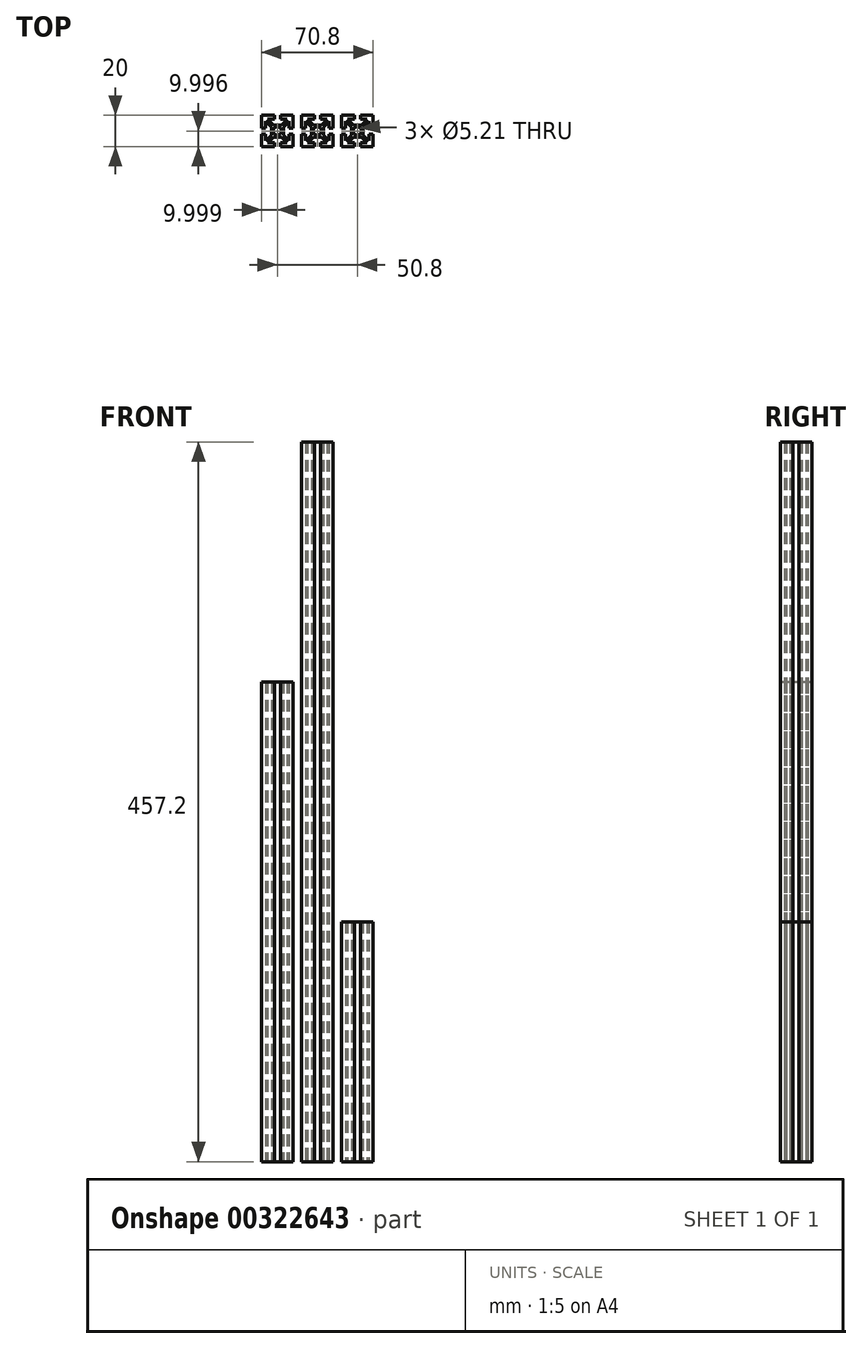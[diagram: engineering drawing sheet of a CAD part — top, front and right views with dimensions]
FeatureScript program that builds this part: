
annotation { "Feature Type Name" : "Feature", "Feature Type Description" : "" }
export const myFeature = defineFeature(function(context is Context, id is Id, definition is map)
    precondition{}
    {
        {
            var Q0;
            Q0=qCreatedBy(makeId("Top.planeOp"),FACE);
            var sketch = newSketch(context, id + "F0", { "sketchPlane" : qUnion([Q0])});
            skCircle(sketch, "E0", {"center": v(-14.24, 3.76) * mm, "radius": 2.6 * mm});
            skLineSegment(sketch, "E1.bottom", {"start": v(-18.05, 7.57) * mm, "end": v(-10.43, 7.57) * mm, "construction": true});
            skLineSegment(sketch, "E1.top", {"start": v(-18.05, -0.05) * mm, "end": v(-10.43, -0.05) * mm, "construction": true});
            skLineSegment(sketch, "E1.left", {"start": v(-18.05, 7.57) * mm, "end": v(-18.05, -0.05) * mm, "construction": true});
            skLineSegment(sketch, "E1.right", {"start": v(-10.43, 7.57) * mm, "end": v(-10.43, -0.05) * mm, "construction": true});
            skPoint(sketch, "E2", {"position": v(-18.05, 3.76) * mm});
            skPoint(sketch, "E3", {"position": v(-14.24, 7.57) * mm});
            skLineSegment(sketch, "E4", {"start": v(-16.78, 7.57) * mm, "end": v(-11.7, 7.57) * mm});
            skLineSegment(sketch, "E5", {"start": v(-11.7, 7.57) * mm, "end": v(-8.05, 11.22) * mm});
            skLineSegment(sketch, "E6", {"start": v(-8.05, 11.22) * mm, "end": v(-12.34, 11.22) * mm});
            skLineSegment(sketch, "E7", {"start": v(-12.34, 11.22) * mm, "end": v(-12.34, 13.76) * mm});
            skLineSegment(sketch, "E8", {"start": v(-12.34, 13.76) * mm, "end": v(-4.24, 13.76) * mm});
            skLineSegment(sketch, "E9", {"start": v(-4.24, 13.76) * mm, "end": v(-4.24, 5.66) * mm});
            skLineSegment(sketch, "E10", {"start": v(-4.24, 5.66) * mm, "end": v(-6.78, 5.66) * mm});
            skLineSegment(sketch, "E11", {"start": v(-6.78, 5.66) * mm, "end": v(-6.78, 9.95) * mm});
            skLineSegment(sketch, "E12", {"start": v(-6.78, 9.95) * mm, "end": v(-10.43, 6.3) * mm});
            skLineSegment(sketch, "E13", {"start": v(-10.43, 6.3) * mm, "end": v(-10.43, 1.22) * mm});
            skLineSegment(sketch, "E14", {"start": v(-10.43, 1.22) * mm, "end": v(-6.78, -2.43) * mm});
            skLineSegment(sketch, "E15", {"start": v(-6.78, -2.43) * mm, "end": v(-6.78, 1.85) * mm});
            skLineSegment(sketch, "E16", {"start": v(-6.78, 1.85) * mm, "end": v(-4.24, 1.85) * mm});
            skLineSegment(sketch, "E17", {"start": v(-4.24, 1.85) * mm, "end": v(-4.24, -6.24) * mm});
            skLineSegment(sketch, "E18", {"start": v(-4.24, -6.24) * mm, "end": v(-12.34, -6.24) * mm});
            skLineSegment(sketch, "E19", {"start": v(-12.34, -6.24) * mm, "end": v(-12.34, -3.7) * mm});
            skLineSegment(sketch, "E20", {"start": v(-12.34, -3.7) * mm, "end": v(-8.05, -3.7) * mm});
            skLineSegment(sketch, "E21", {"start": v(-8.05, -3.7) * mm, "end": v(-11.7, -0.05) * mm});
            skLineSegment(sketch, "E22", {"start": v(-11.7, -0.05) * mm, "end": v(-16.78, -0.05) * mm});
            skLineSegment(sketch, "E23", {"start": v(-16.78, -0.05) * mm, "end": v(-20.43, -3.7) * mm});
            skLineSegment(sketch, "E24", {"start": v(-20.43, -3.7) * mm, "end": v(-16.15, -3.7) * mm});
            skLineSegment(sketch, "E25", {"start": v(-16.15, -3.7) * mm, "end": v(-16.15, -6.24) * mm});
            skLineSegment(sketch, "E26", {"start": v(-16.15, -6.24) * mm, "end": v(-24.24, -6.24) * mm});
            skLineSegment(sketch, "E27", {"start": v(-24.24, -6.24) * mm, "end": v(-24.24, 1.85) * mm});
            skLineSegment(sketch, "E28", {"start": v(-24.24, 1.85) * mm, "end": v(-21.7, 1.85) * mm});
            skLineSegment(sketch, "E29", {"start": v(-21.7, 1.85) * mm, "end": v(-21.7, -2.43) * mm});
            skLineSegment(sketch, "E30", {"start": v(-21.7, -2.43) * mm, "end": v(-18.05, 1.22) * mm});
            skLineSegment(sketch, "E31", {"start": v(-18.05, 1.22) * mm, "end": v(-18.05, 6.3) * mm});
            skLineSegment(sketch, "E32", {"start": v(-18.05, 6.3) * mm, "end": v(-21.7, 9.95) * mm});
            skLineSegment(sketch, "E33", {"start": v(-21.7, 9.95) * mm, "end": v(-21.7, 5.66) * mm});
            skLineSegment(sketch, "E34", {"start": v(-21.7, 5.66) * mm, "end": v(-24.24, 5.66) * mm});
            skLineSegment(sketch, "E35", {"start": v(-24.24, 5.66) * mm, "end": v(-24.24, 13.76) * mm});
            skLineSegment(sketch, "E36", {"start": v(-24.24, 13.76) * mm, "end": v(-16.15, 13.76) * mm});
            skLineSegment(sketch, "E37", {"start": v(-16.15, 13.76) * mm, "end": v(-16.15, 11.22) * mm});
            skLineSegment(sketch, "E38", {"start": v(-16.15, 11.22) * mm, "end": v(-20.43, 11.22) * mm});
            skLineSegment(sketch, "E39", {"start": v(-20.43, 11.22) * mm, "end": v(-16.78, 7.57) * mm});
            skLineSegment(sketch, "E40", {"start": v(-16.15, 13.76) * mm, "end": v(-12.34, 13.76) * mm, "construction": true});
            skLineSegment(sketch, "E41", {"start": v(-4.24, 5.66) * mm, "end": v(-4.24, 1.85) * mm, "construction": true});
            skLineSegment(sketch, "E42", {"start": v(-12.34, -6.24) * mm, "end": v(-16.15, -6.24) * mm, "construction": true});
            skLineSegment(sketch, "E43", {"start": v(-24.24, 1.85) * mm, "end": v(-24.24, 5.66) * mm, "construction": true});
            skPoint(sketch, "E44", {"position": v(-24.24, 3.76) * mm});
            skPoint(sketch, "E45", {"position": v(-14.24, 13.76) * mm});
            skPoint(sketch, "E46", {"position": v(-4.24, 3.76) * mm});
            skPoint(sketch, "E47", {"position": v(-14.24, -6.24) * mm});
            skPoint(sketch, "E48.1.0.0", {"position": v(21.16, 3.76) * mm});
            skLineSegment(sketch, "E48.1.0.1", {"start": v(1.16, 13.76) * mm, "end": v(9.25, 13.76) * mm});
            skPoint(sketch, "E48.1.0.2", {"position": v(11.16, 13.76) * mm});
            skPoint(sketch, "E48.1.0.3", {"position": v(1.16, 3.76) * mm});
            skPoint(sketch, "E48.1.0.4", {"position": v(11.16, -6.24) * mm});
            skCircle(sketch, "E48.1.0.5", {"center": v(11.16, 3.76) * mm, "radius": 2.6 * mm});
            skPoint(sketch, "E48.1.0.6", {"position": v(11.16, 7.57) * mm});
            skLineSegment(sketch, "E48.1.0.7", {"start": v(18.62, -2.43) * mm, "end": v(18.62, 1.85) * mm});
            skPoint(sketch, "E48.1.0.8", {"position": v(7.35, 3.76) * mm});
            skLineSegment(sketch, "E48.1.0.9", {"start": v(7.35, -0.05) * mm, "end": v(14.97, -0.05) * mm, "construction": true});
            skLineSegment(sketch, "E48.1.0.10", {"start": v(21.16, 13.76) * mm, "end": v(21.16, 5.66) * mm});
            skLineSegment(sketch, "E48.1.0.11", {"start": v(13.06, 13.76) * mm, "end": v(21.16, 13.76) * mm});
            skLineSegment(sketch, "E48.1.0.12", {"start": v(18.62, 5.66) * mm, "end": v(18.62, 9.95) * mm});
            skLineSegment(sketch, "E48.1.0.13", {"start": v(21.16, 1.85) * mm, "end": v(21.16, -6.24) * mm});
            skLineSegment(sketch, "E48.1.0.14", {"start": v(21.16, -6.24) * mm, "end": v(13.06, -6.24) * mm});
            skLineSegment(sketch, "E48.1.0.15", {"start": v(9.25, -6.24) * mm, "end": v(1.16, -6.24) * mm});
            skLineSegment(sketch, "E48.1.0.16", {"start": v(1.16, 5.66) * mm, "end": v(1.16, 13.76) * mm});
            skLineSegment(sketch, "E48.1.0.17", {"start": v(1.16, -6.24) * mm, "end": v(1.16, 1.85) * mm});
            skLineSegment(sketch, "E48.1.0.18", {"start": v(3.7, 1.85) * mm, "end": v(3.7, -2.43) * mm});
            skLineSegment(sketch, "E48.1.0.19", {"start": v(14.97, 1.22) * mm, "end": v(18.62, -2.43) * mm});
            skLineSegment(sketch, "E48.1.0.20", {"start": v(3.7, 9.95) * mm, "end": v(3.7, 5.66) * mm});
            skLineSegment(sketch, "E48.1.0.21", {"start": v(14.97, 7.57) * mm, "end": v(14.97, -0.05) * mm, "construction": true});
            skLineSegment(sketch, "E48.1.0.22", {"start": v(7.35, 7.57) * mm, "end": v(7.35, -0.05) * mm, "construction": true});
            skLineSegment(sketch, "E48.1.0.23", {"start": v(13.7, -0.05) * mm, "end": v(8.62, -0.05) * mm});
            skLineSegment(sketch, "E48.1.0.24", {"start": v(7.35, 7.57) * mm, "end": v(14.97, 7.57) * mm, "construction": true});
            skLineSegment(sketch, "E48.1.0.25", {"start": v(13.7, 7.57) * mm, "end": v(17.35, 11.22) * mm});
            skLineSegment(sketch, "E48.1.0.26", {"start": v(7.35, 1.22) * mm, "end": v(7.35, 6.3) * mm});
            skLineSegment(sketch, "E48.1.0.27", {"start": v(8.62, -0.05) * mm, "end": v(4.97, -3.7) * mm});
            skLineSegment(sketch, "E48.1.0.28", {"start": v(9.25, 11.22) * mm, "end": v(4.97, 11.22) * mm});
            skLineSegment(sketch, "E48.1.0.29", {"start": v(21.16, 5.66) * mm, "end": v(18.62, 5.66) * mm});
            skLineSegment(sketch, "E48.1.0.30", {"start": v(1.16, 1.85) * mm, "end": v(3.7, 1.85) * mm});
            skLineSegment(sketch, "E48.1.0.31", {"start": v(9.25, 13.76) * mm, "end": v(9.25, 11.22) * mm});
            skLineSegment(sketch, "E48.1.0.32", {"start": v(8.62, 7.57) * mm, "end": v(13.7, 7.57) * mm});
            skLineSegment(sketch, "E48.1.0.33", {"start": v(18.62, 1.85) * mm, "end": v(21.16, 1.85) * mm});
            skLineSegment(sketch, "E48.1.0.34", {"start": v(4.97, 11.22) * mm, "end": v(8.62, 7.57) * mm});
            skLineSegment(sketch, "E48.1.0.35", {"start": v(13.06, 11.22) * mm, "end": v(13.06, 13.76) * mm});
            skLineSegment(sketch, "E48.1.0.36", {"start": v(7.35, 6.3) * mm, "end": v(3.7, 9.95) * mm});
            skLineSegment(sketch, "E48.1.0.37", {"start": v(17.35, 11.22) * mm, "end": v(13.06, 11.22) * mm});
            skLineSegment(sketch, "E48.1.0.38", {"start": v(4.97, -3.7) * mm, "end": v(9.25, -3.7) * mm});
            skLineSegment(sketch, "E48.1.0.39", {"start": v(3.7, 5.66) * mm, "end": v(1.16, 5.66) * mm});
            skLineSegment(sketch, "E48.1.0.40", {"start": v(13.06, -3.7) * mm, "end": v(17.35, -3.7) * mm});
            skLineSegment(sketch, "E48.1.0.41", {"start": v(17.35, -3.7) * mm, "end": v(13.7, -0.05) * mm});
            skLineSegment(sketch, "E48.1.0.42", {"start": v(3.7, -2.43) * mm, "end": v(7.35, 1.22) * mm});
            skLineSegment(sketch, "E48.1.0.43", {"start": v(18.62, 9.95) * mm, "end": v(14.97, 6.3) * mm});
            skLineSegment(sketch, "E48.1.0.44", {"start": v(14.97, 6.3) * mm, "end": v(14.97, 1.22) * mm});
            skLineSegment(sketch, "E48.1.0.45", {"start": v(1.16, 1.85) * mm, "end": v(1.16, 5.66) * mm, "construction": true});
            skLineSegment(sketch, "E48.1.0.46", {"start": v(13.06, -6.24) * mm, "end": v(13.06, -3.7) * mm});
            skLineSegment(sketch, "E48.1.0.47", {"start": v(9.25, 13.76) * mm, "end": v(13.06, 13.76) * mm, "construction": true});
            skLineSegment(sketch, "E48.1.0.48", {"start": v(9.25, -3.7) * mm, "end": v(9.25, -6.24) * mm});
            skLineSegment(sketch, "E48.1.0.49", {"start": v(21.16, 5.66) * mm, "end": v(21.16, 1.85) * mm, "construction": true});
            skLineSegment(sketch, "E48.1.0.50", {"start": v(13.06, -6.24) * mm, "end": v(9.25, -6.24) * mm, "construction": true});
            skPoint(sketch, "E48.2.0.0", {"position": v(46.56, 3.76) * mm});
            skLineSegment(sketch, "E48.2.0.1", {"start": v(26.56, 13.76) * mm, "end": v(34.65, 13.76) * mm});
            skPoint(sketch, "E48.2.0.2", {"position": v(36.56, 13.76) * mm});
            skPoint(sketch, "E48.2.0.3", {"position": v(26.56, 3.76) * mm});
            skPoint(sketch, "E48.2.0.4", {"position": v(36.56, -6.24) * mm});
            skCircle(sketch, "E48.2.0.5", {"center": v(36.56, 3.76) * mm, "radius": 2.6 * mm});
            skPoint(sketch, "E48.2.0.6", {"position": v(36.56, 7.57) * mm});
            skLineSegment(sketch, "E48.2.0.7", {"start": v(44.02, -2.43) * mm, "end": v(44.02, 1.85) * mm});
            skPoint(sketch, "E48.2.0.8", {"position": v(32.75, 3.76) * mm});
            skLineSegment(sketch, "E48.2.0.9", {"start": v(32.75, -0.05) * mm, "end": v(40.37, -0.05) * mm, "construction": true});
            skLineSegment(sketch, "E48.2.0.10", {"start": v(46.56, 13.76) * mm, "end": v(46.56, 5.66) * mm});
            skLineSegment(sketch, "E48.2.0.11", {"start": v(38.46, 13.76) * mm, "end": v(46.56, 13.76) * mm});
            skLineSegment(sketch, "E48.2.0.12", {"start": v(44.02, 5.66) * mm, "end": v(44.02, 9.95) * mm});
            skLineSegment(sketch, "E48.2.0.13", {"start": v(46.56, 1.85) * mm, "end": v(46.56, -6.24) * mm});
            skLineSegment(sketch, "E48.2.0.14", {"start": v(46.56, -6.24) * mm, "end": v(38.46, -6.24) * mm});
            skLineSegment(sketch, "E48.2.0.15", {"start": v(34.65, -6.24) * mm, "end": v(26.56, -6.24) * mm});
            skLineSegment(sketch, "E48.2.0.16", {"start": v(26.56, 5.66) * mm, "end": v(26.56, 13.76) * mm});
            skLineSegment(sketch, "E48.2.0.17", {"start": v(26.56, -6.24) * mm, "end": v(26.56, 1.85) * mm});
            skLineSegment(sketch, "E48.2.0.18", {"start": v(29.1, 1.85) * mm, "end": v(29.1, -2.43) * mm});
            skLineSegment(sketch, "E48.2.0.19", {"start": v(40.37, 1.22) * mm, "end": v(44.02, -2.43) * mm});
            skLineSegment(sketch, "E48.2.0.20", {"start": v(29.1, 9.95) * mm, "end": v(29.1, 5.66) * mm});
            skLineSegment(sketch, "E48.2.0.21", {"start": v(40.37, 7.57) * mm, "end": v(40.37, -0.05) * mm, "construction": true});
            skLineSegment(sketch, "E48.2.0.22", {"start": v(32.75, 7.57) * mm, "end": v(32.75, -0.05) * mm, "construction": true});
            skLineSegment(sketch, "E48.2.0.23", {"start": v(39.1, -0.05) * mm, "end": v(34.02, -0.05) * mm});
            skLineSegment(sketch, "E48.2.0.24", {"start": v(32.75, 7.57) * mm, "end": v(40.37, 7.57) * mm, "construction": true});
            skLineSegment(sketch, "E48.2.0.25", {"start": v(39.1, 7.57) * mm, "end": v(42.75, 11.22) * mm});
            skLineSegment(sketch, "E48.2.0.26", {"start": v(32.75, 1.22) * mm, "end": v(32.75, 6.3) * mm});
            skLineSegment(sketch, "E48.2.0.27", {"start": v(34.02, -0.05) * mm, "end": v(30.37, -3.7) * mm});
            skLineSegment(sketch, "E48.2.0.28", {"start": v(34.65, 11.22) * mm, "end": v(30.37, 11.22) * mm});
            skLineSegment(sketch, "E48.2.0.29", {"start": v(46.56, 5.66) * mm, "end": v(44.02, 5.66) * mm});
            skLineSegment(sketch, "E48.2.0.30", {"start": v(26.56, 1.85) * mm, "end": v(29.1, 1.85) * mm});
            skLineSegment(sketch, "E48.2.0.31", {"start": v(34.65, 13.76) * mm, "end": v(34.65, 11.22) * mm});
            skLineSegment(sketch, "E48.2.0.32", {"start": v(34.02, 7.57) * mm, "end": v(39.1, 7.57) * mm});
            skLineSegment(sketch, "E48.2.0.33", {"start": v(44.02, 1.85) * mm, "end": v(46.56, 1.85) * mm});
            skLineSegment(sketch, "E48.2.0.34", {"start": v(30.37, 11.22) * mm, "end": v(34.02, 7.57) * mm});
            skLineSegment(sketch, "E48.2.0.35", {"start": v(38.46, 11.22) * mm, "end": v(38.46, 13.76) * mm});
            skLineSegment(sketch, "E48.2.0.36", {"start": v(32.75, 6.3) * mm, "end": v(29.1, 9.95) * mm});
            skLineSegment(sketch, "E48.2.0.37", {"start": v(42.75, 11.22) * mm, "end": v(38.46, 11.22) * mm});
            skLineSegment(sketch, "E48.2.0.38", {"start": v(30.37, -3.7) * mm, "end": v(34.65, -3.7) * mm});
            skLineSegment(sketch, "E48.2.0.39", {"start": v(29.1, 5.66) * mm, "end": v(26.56, 5.66) * mm});
            skLineSegment(sketch, "E48.2.0.40", {"start": v(38.46, -3.7) * mm, "end": v(42.75, -3.7) * mm});
            skLineSegment(sketch, "E48.2.0.41", {"start": v(42.75, -3.7) * mm, "end": v(39.1, -0.05) * mm});
            skLineSegment(sketch, "E48.2.0.42", {"start": v(29.1, -2.43) * mm, "end": v(32.75, 1.22) * mm});
            skLineSegment(sketch, "E48.2.0.43", {"start": v(44.02, 9.95) * mm, "end": v(40.37, 6.3) * mm});
            skLineSegment(sketch, "E48.2.0.44", {"start": v(40.37, 6.3) * mm, "end": v(40.37, 1.22) * mm});
            skLineSegment(sketch, "E48.2.0.45", {"start": v(26.56, 1.85) * mm, "end": v(26.56, 5.66) * mm, "construction": true});
            skLineSegment(sketch, "E48.2.0.46", {"start": v(38.46, -6.24) * mm, "end": v(38.46, -3.7) * mm});
            skLineSegment(sketch, "E48.2.0.47", {"start": v(34.65, 13.76) * mm, "end": v(38.46, 13.76) * mm, "construction": true});
            skLineSegment(sketch, "E48.2.0.48", {"start": v(34.65, -3.7) * mm, "end": v(34.65, -6.24) * mm});
            skLineSegment(sketch, "E48.2.0.49", {"start": v(46.56, 5.66) * mm, "end": v(46.56, 1.85) * mm, "construction": true});
            skLineSegment(sketch, "E48.2.0.50", {"start": v(38.46, -6.24) * mm, "end": v(34.65, -6.24) * mm, "construction": true});
            skPoint(sketch, "E48.3.0.0", {"position": v(71.96, 3.76) * mm});
            skLineSegment(sketch, "E48.3.0.1", {"start": v(51.96, 13.76) * mm, "end": v(60.05, 13.76) * mm});
            skPoint(sketch, "E48.3.0.2", {"position": v(61.96, 13.76) * mm});
            skPoint(sketch, "E48.3.0.3", {"position": v(51.96, 3.76) * mm});
            skPoint(sketch, "E48.3.0.4", {"position": v(61.96, -6.24) * mm});
            skCircle(sketch, "E48.3.0.5", {"center": v(61.96, 3.76) * mm, "radius": 2.6 * mm});
            skPoint(sketch, "E48.3.0.6", {"position": v(61.96, 7.57) * mm});
            skLineSegment(sketch, "E48.3.0.7", {"start": v(69.42, -2.43) * mm, "end": v(69.42, 1.85) * mm});
            skPoint(sketch, "E48.3.0.8", {"position": v(58.15, 3.76) * mm});
            skLineSegment(sketch, "E48.3.0.9", {"start": v(58.15, -0.05) * mm, "end": v(65.77, -0.05) * mm, "construction": true});
            skLineSegment(sketch, "E48.3.0.10", {"start": v(71.96, 13.76) * mm, "end": v(71.96, 5.66) * mm});
            skLineSegment(sketch, "E48.3.0.11", {"start": v(63.86, 13.76) * mm, "end": v(71.96, 13.76) * mm});
            skLineSegment(sketch, "E48.3.0.12", {"start": v(69.42, 5.66) * mm, "end": v(69.42, 9.95) * mm});
            skLineSegment(sketch, "E48.3.0.13", {"start": v(71.96, 1.85) * mm, "end": v(71.96, -6.24) * mm});
            skLineSegment(sketch, "E48.3.0.14", {"start": v(71.96, -6.24) * mm, "end": v(63.86, -6.24) * mm});
            skLineSegment(sketch, "E48.3.0.15", {"start": v(60.05, -6.24) * mm, "end": v(51.96, -6.24) * mm});
            skLineSegment(sketch, "E48.3.0.16", {"start": v(51.96, 5.66) * mm, "end": v(51.96, 13.76) * mm});
            skLineSegment(sketch, "E48.3.0.17", {"start": v(51.96, -6.24) * mm, "end": v(51.96, 1.85) * mm});
            skLineSegment(sketch, "E48.3.0.18", {"start": v(54.5, 1.85) * mm, "end": v(54.5, -2.43) * mm});
            skLineSegment(sketch, "E48.3.0.19", {"start": v(65.77, 1.22) * mm, "end": v(69.42, -2.43) * mm});
            skLineSegment(sketch, "E48.3.0.20", {"start": v(54.5, 9.95) * mm, "end": v(54.5, 5.66) * mm});
            skLineSegment(sketch, "E48.3.0.21", {"start": v(65.77, 7.57) * mm, "end": v(65.77, -0.05) * mm, "construction": true});
            skLineSegment(sketch, "E48.3.0.22", {"start": v(58.15, 7.57) * mm, "end": v(58.15, -0.05) * mm, "construction": true});
            skLineSegment(sketch, "E48.3.0.23", {"start": v(64.5, -0.05) * mm, "end": v(59.42, -0.05) * mm});
            skLineSegment(sketch, "E48.3.0.24", {"start": v(58.15, 7.57) * mm, "end": v(65.77, 7.57) * mm, "construction": true});
            skLineSegment(sketch, "E48.3.0.25", {"start": v(64.5, 7.57) * mm, "end": v(68.15, 11.22) * mm});
            skLineSegment(sketch, "E48.3.0.26", {"start": v(58.15, 1.22) * mm, "end": v(58.15, 6.3) * mm});
            skLineSegment(sketch, "E48.3.0.27", {"start": v(59.42, -0.05) * mm, "end": v(55.77, -3.7) * mm});
            skLineSegment(sketch, "E48.3.0.28", {"start": v(60.05, 11.22) * mm, "end": v(55.77, 11.22) * mm});
            skLineSegment(sketch, "E48.3.0.29", {"start": v(71.96, 5.66) * mm, "end": v(69.42, 5.66) * mm});
            skLineSegment(sketch, "E48.3.0.30", {"start": v(51.96, 1.85) * mm, "end": v(54.5, 1.85) * mm});
            skLineSegment(sketch, "E48.3.0.31", {"start": v(60.05, 13.76) * mm, "end": v(60.05, 11.22) * mm});
            skLineSegment(sketch, "E48.3.0.32", {"start": v(59.42, 7.57) * mm, "end": v(64.5, 7.57) * mm});
            skLineSegment(sketch, "E48.3.0.33", {"start": v(69.42, 1.85) * mm, "end": v(71.96, 1.85) * mm});
            skLineSegment(sketch, "E48.3.0.34", {"start": v(55.77, 11.22) * mm, "end": v(59.42, 7.57) * mm});
            skLineSegment(sketch, "E48.3.0.35", {"start": v(63.86, 11.22) * mm, "end": v(63.86, 13.76) * mm});
            skLineSegment(sketch, "E48.3.0.36", {"start": v(58.15, 6.3) * mm, "end": v(54.5, 9.95) * mm});
            skLineSegment(sketch, "E48.3.0.37", {"start": v(68.15, 11.22) * mm, "end": v(63.86, 11.22) * mm});
            skLineSegment(sketch, "E48.3.0.38", {"start": v(55.77, -3.7) * mm, "end": v(60.05, -3.7) * mm});
            skLineSegment(sketch, "E48.3.0.39", {"start": v(54.5, 5.66) * mm, "end": v(51.96, 5.66) * mm});
            skLineSegment(sketch, "E48.3.0.40", {"start": v(63.86, -3.7) * mm, "end": v(68.15, -3.7) * mm});
            skLineSegment(sketch, "E48.3.0.41", {"start": v(68.15, -3.7) * mm, "end": v(64.5, -0.05) * mm});
            skLineSegment(sketch, "E48.3.0.42", {"start": v(54.5, -2.43) * mm, "end": v(58.15, 1.22) * mm});
            skLineSegment(sketch, "E48.3.0.43", {"start": v(69.42, 9.95) * mm, "end": v(65.77, 6.3) * mm});
            skLineSegment(sketch, "E48.3.0.44", {"start": v(65.77, 6.3) * mm, "end": v(65.77, 1.22) * mm});
            skLineSegment(sketch, "E48.3.0.45", {"start": v(51.96, 1.85) * mm, "end": v(51.96, 5.66) * mm, "construction": true});
            skLineSegment(sketch, "E48.3.0.46", {"start": v(63.86, -6.24) * mm, "end": v(63.86, -3.7) * mm});
            skLineSegment(sketch, "E48.3.0.47", {"start": v(60.05, 13.76) * mm, "end": v(63.86, 13.76) * mm, "construction": true});
            skLineSegment(sketch, "E48.3.0.48", {"start": v(60.05, -3.7) * mm, "end": v(60.05, -6.24) * mm});
            skLineSegment(sketch, "E48.3.0.49", {"start": v(71.96, 5.66) * mm, "end": v(71.96, 1.85) * mm, "construction": true});
            skLineSegment(sketch, "E48.3.0.50", {"start": v(63.86, -6.24) * mm, "end": v(60.05, -6.24) * mm, "construction": true});
            skLineSegment(sketch, "E48.direction1", {"start": v(-24.24, -6.24) * mm, "end": v(1.16, -6.24) * mm, "construction": true});
            skSolve(sketch);
        }
        {
            var Q0;
            Q0=makeQuery(id+"F0.imprint","IMPRINT",FACE,{"disambiguationData":[TD([[makeQuery(id+"F0.imprint","IMPRINT",EDGE,{"derivedFrom":sQuery(id+"F0.wireOp",EDGE,"E0")}),-1.0]])]});
            extrude(context, id + "F1", {"entities" : qUnion([Q0]), "depth" : 304.8 * mm});
        }
        {
            var Q0;
            Q0=makeQuery(id+"F0.imprint","IMPRINT",FACE,{"disambiguationData":[TD([[makeQuery(id+"F0.imprint","IMPRINT",EDGE,{"derivedFrom":sQuery(id+"F0.wireOp",EDGE,"E48.1.0.1")}),-1.0]])]});
            extrude(context, id + "F2", {"entities" : qUnion([Q0]), "depth" : 457.2 * mm});
        }
        {
            var Q0;
            Q0=makeQuery(id+"F0.imprint","IMPRINT",FACE,{"disambiguationData":[TD([[makeQuery(id+"F0.imprint","IMPRINT",EDGE,{"derivedFrom":sQuery(id+"F0.wireOp",EDGE,"E48.2.0.1")}),-1.0]])]});
            extrude(context, id + "F3", {"entities" : qUnion([Q0]), "depth" : 152.4 * mm});
        }
    });
